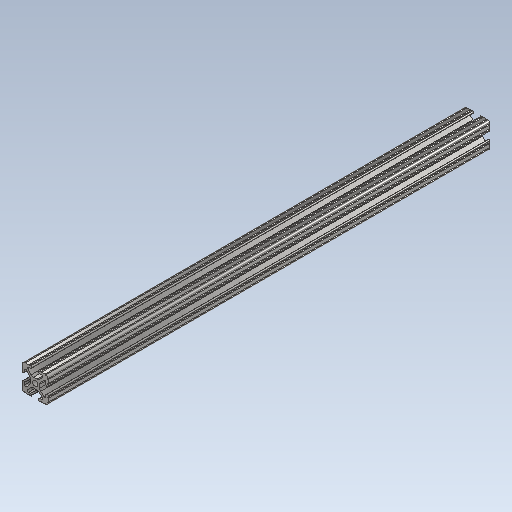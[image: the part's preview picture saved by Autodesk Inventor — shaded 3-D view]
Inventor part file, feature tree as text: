
AUTODESK INVENTOR PART (.ipt)
format: ipt  version: 2020 (Build 240168000, 168)  size: 281,600 bytes
history: native  units: in
note: dims shown in document units (in); Inventor stores cm internally (conversion verified against a paired STEP export)
features: other x3, sketch x1
ambient origin geometry x8: Origin, YZ Plane, XZ Plane, XY Plane, X Axis, Y Axis, Z Axis, Center Point
bodies: Solid1 (feature_tree)
feature tree (4):
  other  "17in 1x1 T slot.ipt"
  other  "Solid1::17in 1x1 T slot.ipt"
  other  "TaggingFeature1"
  sketch  "Sketch1"  dims[d0=0.3937in]
